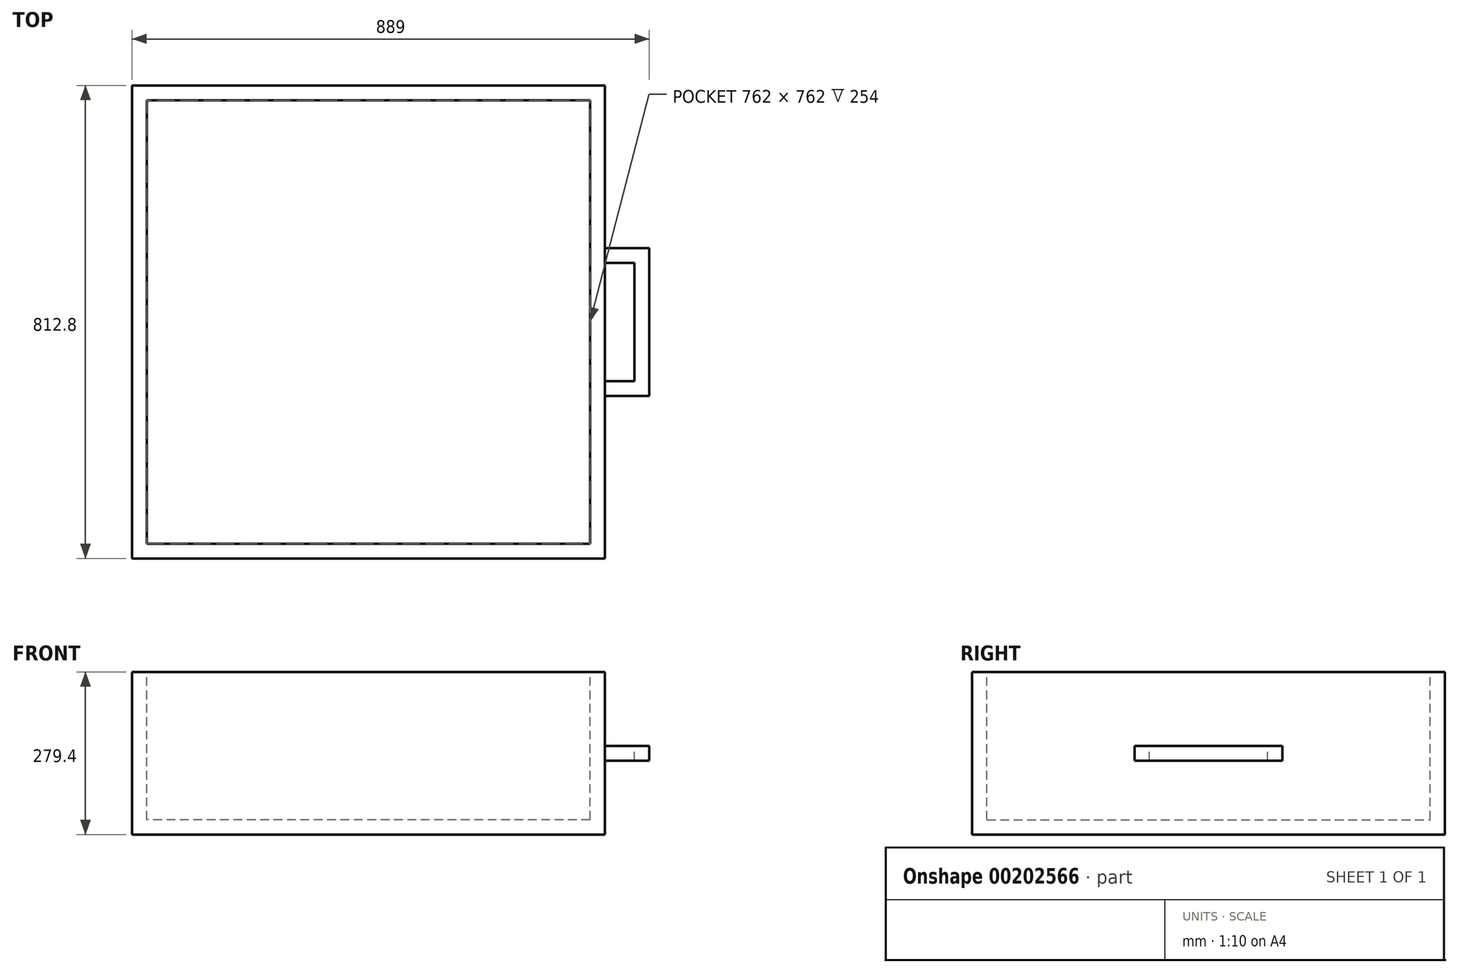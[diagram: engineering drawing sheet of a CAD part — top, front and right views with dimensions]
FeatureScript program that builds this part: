
annotation { "Feature Type Name" : "Feature", "Feature Type Description" : "" }
export const myFeature = defineFeature(function(context is Context, id is Id, definition is map)
    precondition{}
    {
        {
            var Q0;
            Q0=qCreatedBy(makeId("Top.planeOp"),FACE);
            var sketch = newSketch(context, id + "F0", { "sketchPlane" : qUnion([Q0])});
            skLineSegment(sketch, "E0.bottom", {"start": v(0, 0) * mm, "end": v(812.8, 0) * mm});
            skLineSegment(sketch, "E0.top", {"start": v(0, 812.8) * mm, "end": v(812.8, 812.8) * mm});
            skLineSegment(sketch, "E0.left", {"start": v(0, 0) * mm, "end": v(0, 812.8) * mm});
            skLineSegment(sketch, "E0.right", {"start": v(812.8, 0) * mm, "end": v(812.8, 812.8) * mm});
            skSolve(sketch);
        }
        {
            var Q0;
            Q0 = qSketchRegion(id + "F0", true);
            extrude(context, id + "F1", {"entities" : qUnion([Q0]), "depth" : 279.4 * mm});
        }
        {
            var Q0;
            Q0=makeQuery(id+"F1.opExtrude","CAP_FACE",FACE,{"disambiguationData":[OSD([sQuery(id+"F0.wireOp",EDGE,"E0.bottom"),sQuery(id+"F0.wireOp",EDGE,"E0.top"),sQuery(id+"F0.wireOp",EDGE,"E0.left"),sQuery(id+"F0.wireOp",EDGE,"E0.right")])],"isStart":false});
            var sketch = newSketch(context, id + "F2", { "sketchPlane" : qUnion([Q0])});
            skLineSegment(sketch, "E1", {"start": v(812.8, 0) * mm, "end": v(787.4, 0) * mm});
            skLineSegment(sketch, "E2", {"start": v(787.4, 0) * mm, "end": v(787.4, 25.4) * mm});
            skLineSegment(sketch, "E3.bottom", {"start": v(787.4, 25.4) * mm, "end": v(25.4, 25.4) * mm});
            skLineSegment(sketch, "E3.top", {"start": v(787.4, 736.6) * mm, "end": v(25.4, 736.6) * mm});
            skLineSegment(sketch, "E3.left", {"start": v(787.4, 25.4) * mm, "end": v(787.4, 736.6) * mm});
            skLineSegment(sketch, "E3.right", {"start": v(25.4, 25.4) * mm, "end": v(25.4, 736.6) * mm});
            skSolve(sketch);
        }
        {
            var Q0;
            Q0=makeQuery(id+"F2.imprint","IMPRINT",FACE,{"disambiguationData":[TD([[makeQuery(id+"F2.imprint","IMPRINT",EDGE,{"derivedFrom":sQuery(id+"F2.wireOp",EDGE,"E3.bottom")}),-1.0]])]});
            extrude(context, id + "F3", {"entities" : qUnion([Q0]), "operationType" : NewBodyOperationType.REMOVE, "oppositeDirection" : true, "depth" : 254 * mm});
        }
        {
            var Q0;
            Q0=makeQuery(id+"F1.opExtrude","SWEPT_FACE",FACE,{"disambiguationData":[OSD([sQuery(id+"F0.wireOp",EDGE,"E0.right")])]});
            var sketch = newSketch(context, id + "F4", { "sketchPlane" : qUnion([Q0])});
            skLineSegment(sketch, "E4", {"start": v(0, 0) * mm, "end": v(0, 127) * mm});
            skLineSegment(sketch, "E5", {"start": v(0, 127) * mm, "end": v(279.4, 127) * mm});
            skLineSegment(sketch, "E6.bottom", {"start": v(279.4, 127) * mm, "end": v(304.8, 127) * mm});
            skLineSegment(sketch, "E6.top", {"start": v(279.4, 152.4) * mm, "end": v(304.8, 152.4) * mm});
            skLineSegment(sketch, "E6.left", {"start": v(279.4, 127) * mm, "end": v(279.4, 152.4) * mm});
            skLineSegment(sketch, "E6.right", {"start": v(304.8, 127) * mm, "end": v(304.8, 152.4) * mm});
            skLineSegment(sketch, "E7", {"start": v(304.8, 127) * mm, "end": v(508, 127) * mm});
            skLineSegment(sketch, "E8.bottom", {"start": v(508, 127) * mm, "end": v(533.4, 127) * mm});
            skLineSegment(sketch, "E8.top", {"start": v(508, 152.4) * mm, "end": v(533.4, 152.4) * mm});
            skLineSegment(sketch, "E8.left", {"start": v(508, 127) * mm, "end": v(508, 152.4) * mm});
            skLineSegment(sketch, "E8.right", {"start": v(533.4, 127) * mm, "end": v(533.4, 152.4) * mm});
            skSolve(sketch);
        }
        {
            var Q0;
            Q0=makeQuery(id+"F4.imprint","IMPRINT",FACE,{"disambiguationData":[TD([[makeQuery(id+"F4.imprint","IMPRINT",EDGE,{"derivedFrom":sQuery(id+"F4.wireOp",EDGE,"E6.bottom")}),1.0]])]});
            var Q1;
            Q1=makeQuery(id+"F4.imprint","IMPRINT",FACE,{"disambiguationData":[TD([[makeQuery(id+"F4.imprint","IMPRINT",EDGE,{"derivedFrom":sQuery(id+"F4.wireOp",EDGE,"E8.bottom")}),1.0]])]});
            extrude(context, id + "F5", {"entities" : qUnion([Q0, Q1]), "operationType" : NewBodyOperationType.ADD, "depth" : 50.8 * mm});
        }
        {
            var Q0;
            Q0=makeQuery(id+"F5.opExtrude","CAP_FACE",FACE,{"disambiguationData":[OSD([sQuery(id+"F4.wireOp",EDGE,"E6.bottom"),sQuery(id+"F4.wireOp",EDGE,"E6.top"),sQuery(id+"F4.wireOp",EDGE,"E6.left"),sQuery(id+"F4.wireOp",EDGE,"E6.right")])],"isStart":false});
            var sketch = newSketch(context, id + "F6", { "sketchPlane" : qUnion([Q0])});
            skLineSegment(sketch, "E9.bottom", {"start": v(279.4, 152.4) * mm, "end": v(533.4, 152.4) * mm});
            skLineSegment(sketch, "E9.top", {"start": v(279.4, 127) * mm, "end": v(533.4, 127) * mm});
            skLineSegment(sketch, "E9.left", {"start": v(279.4, 152.4) * mm, "end": v(279.4, 127) * mm});
            skLineSegment(sketch, "E9.right", {"start": v(533.4, 152.4) * mm, "end": v(533.4, 127) * mm});
            skSolve(sketch);
        }
        {
            var Q0;
            {var subQ2=sQuery(id+"F6.wireOp",EDGE,"E9.right");Q0=makeQuery(id+"F6.imprint","IMPRINT",FACE,{"disambiguationData":[TD([[makeQuery(id+"F6.imprint","IMPRINT",EDGE,{"derivedFrom":subQ2}),-1.0]])]});}
            var Q1;
            {var subQ0=sQuery(id+"F6.wireOp",EDGE,"E9.left");Q1=makeQuery(id+"F6.imprint","IMPRINT",FACE,{"disambiguationData":[TD([[makeQuery(id+"F6.imprint","IMPRINT",EDGE,{"derivedFrom":subQ0}),-1.0]])]});}
            extrude(context, id + "F7", {"entities" : qUnion([Q0, Q1]), "operationType" : NewBodyOperationType.ADD, "depth" : 25.4 * mm});
        }
        {
            var Q0;
            Q0=makeQuery(id+"F1.opExtrude","CAP_FACE",FACE,{"disambiguationData":[OSD([sQuery(id+"F0.wireOp",EDGE,"E0.bottom"),sQuery(id+"F0.wireOp",EDGE,"E0.top"),sQuery(id+"F0.wireOp",EDGE,"E0.left"),sQuery(id+"F0.wireOp",EDGE,"E0.right")])],"isStart":false});
            var sketch = newSketch(context, id + "F8", { "sketchPlane" : qUnion([Q0])});
            skLineSegment(sketch, "E10.bottom", {"start": v(25.4, 736.6) * mm, "end": v(787.4, 736.6) * mm});
            skLineSegment(sketch, "E10.top", {"start": v(25.4, 787.4) * mm, "end": v(787.4, 787.4) * mm});
            skLineSegment(sketch, "E10.left", {"start": v(25.4, 736.6) * mm, "end": v(25.4, 787.4) * mm});
            skLineSegment(sketch, "E10.right", {"start": v(787.4, 736.6) * mm, "end": v(787.4, 787.4) * mm});
            skSolve(sketch);
        }
        {
            var Q0;
            Q0=makeQuery(id+"F8.imprint","IMPRINT",FACE,{"disambiguationData":[TD([[makeQuery(id+"F8.imprint","IMPRINT",EDGE,{"derivedFrom":sQuery(id+"F8.wireOp",EDGE,"E10.bottom")}),-1.0]])]});
            extrude(context, id + "F9", {"entities" : qUnion([Q0]), "operationType" : NewBodyOperationType.REMOVE, "oppositeDirection" : true, "depth" : 254 * mm});
        }
    });
